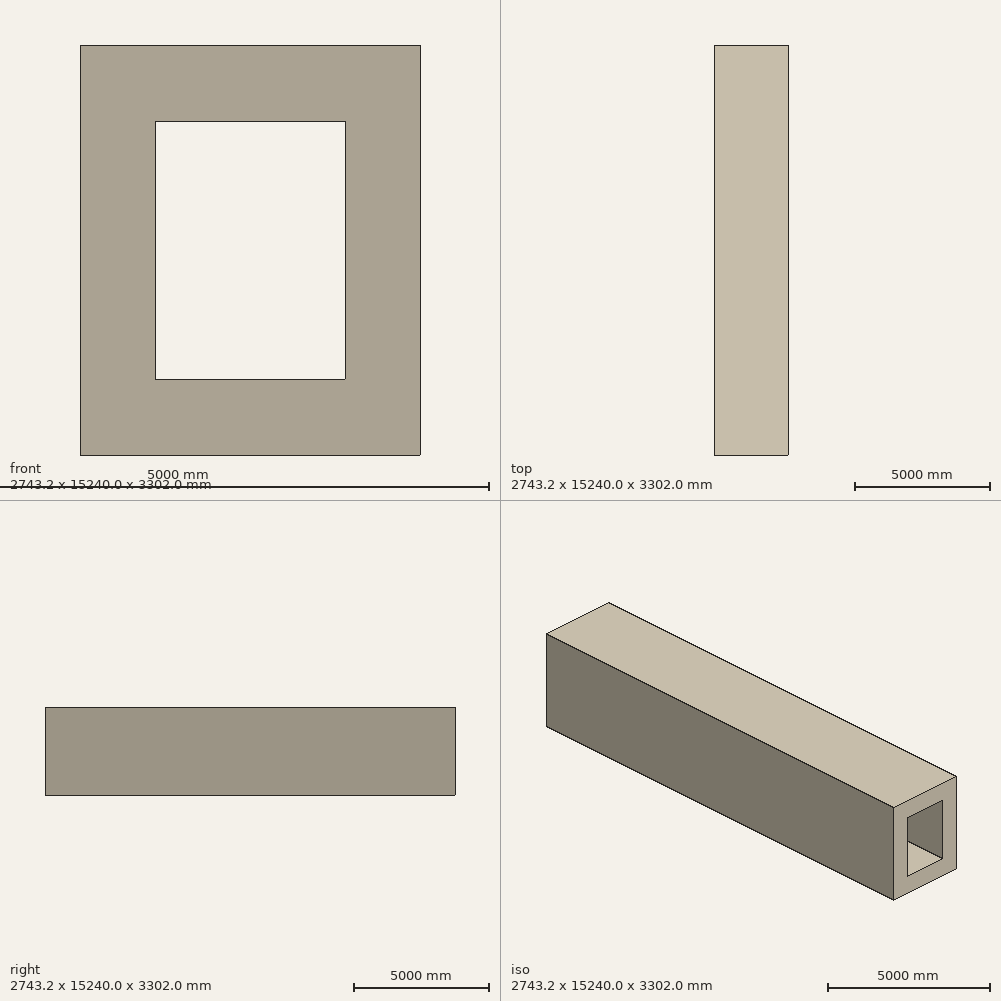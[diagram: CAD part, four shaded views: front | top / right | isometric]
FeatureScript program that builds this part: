
annotation { "Feature Type Name" : "Feature", "Feature Type Description" : "" }
export const myFeature = defineFeature(function(context is Context, id is Id, definition is map)
    precondition{}
    {
        {
            var Q0;
            Q0=qCreatedBy(makeId("Front.planeOp"),FACE);
            var sketch = newSketch(context, id + "F0", { "sketchPlane" : qUnion([Q0])});
            skLineSegment(sketch, "E0.bottom", {"start": v(-762, -1041.4) * mm, "end": v(762, -1041.4) * mm});
            skLineSegment(sketch, "E0.top", {"start": v(-762, 1041.4) * mm, "end": v(762, 1041.4) * mm});
            skLineSegment(sketch, "E0.left", {"start": v(-762, -1041.4) * mm, "end": v(-762, 1041.4) * mm});
            skLineSegment(sketch, "E0.right", {"start": v(762, -1041.4) * mm, "end": v(762, 1041.4) * mm});
            skLineSegment(sketch, "E1.bottom", {"start": v(-1371.6, 1651) * mm, "end": v(1371.6, 1651) * mm});
            skLineSegment(sketch, "E1.top", {"start": v(-1371.6, -1651) * mm, "end": v(1371.6, -1651) * mm});
            skLineSegment(sketch, "E1.left", {"start": v(-1371.6, 1651) * mm, "end": v(-1371.6, -1651) * mm});
            skLineSegment(sketch, "E1.right", {"start": v(1371.6, 1651) * mm, "end": v(1371.6, -1651) * mm});
            skSolve(sketch);
        }
        {
            var Q0;
            Q0 = qSketchRegion(id + "F0", true);
            extrude(context, id + "F1", {"entities" : qUnion([Q0]), "depth" : 15240 * mm, "offsetDistance" : 25.4 * mm});
        }
    });
